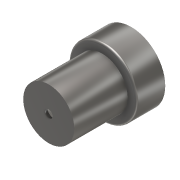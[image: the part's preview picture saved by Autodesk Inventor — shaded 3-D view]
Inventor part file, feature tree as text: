
AUTODESK INVENTOR PART (.ipt)
format: ipt  version: 2017 (Build 210142000, 142)  size: 172,544 bytes
history: native  units: mm
features: sketch x5, sweep x2, revolve x1, fillet x1, projected_geometry x1
ambient origin geometry x8: Origin, YZ Plane, XZ Plane, XY Plane, X Axis, Y Axis, Z Axis, Center Point
bodies: Solid1 (feature_tree)
feature tree (10):
  revolve  "Revolution1"  [1 undecoded]
  fillet  "Fillet1"  Radius=14.0mm
  sweep  "Sweep2"
  sweep  "Sweep3"
  sketch  "Sketch1"  dims[d0=5.0mm d1=6.0mm d2=14.0mm]
  sketch  "Sketch4"  dims[d3=11.0mm d4=2.0mm]
  sketch  "Sketch5"  dims[d5=4.0mm d6=10.5mm]
  sketch  "Sketch6"  dims[d7=3.0mm]
  sketch  "Sketch7"  dims[d8=8.5mm d11=0.8mm d12=90.0deg d13=0.5mm d25=1.3mm d26=1.3mm d28=1.5mm d29=1.5mm d30=11.0mm d31=2.15mm d32=2.15mm d33=1.0mm d34=1.0mm d35=0.0mm d36=0.0mm d37=1.3mm d38=11.0mm d39=1.0mm d40=2.15mm d41=0.0mm d42=0.0mm]
  projected_geometry  "Projected Loop2"
note: 1 required parameter value undecoded (feature->parameter linkage not recoverable at this tier; creation-order binding heuristic only, values carry confidence <= 0.55)
